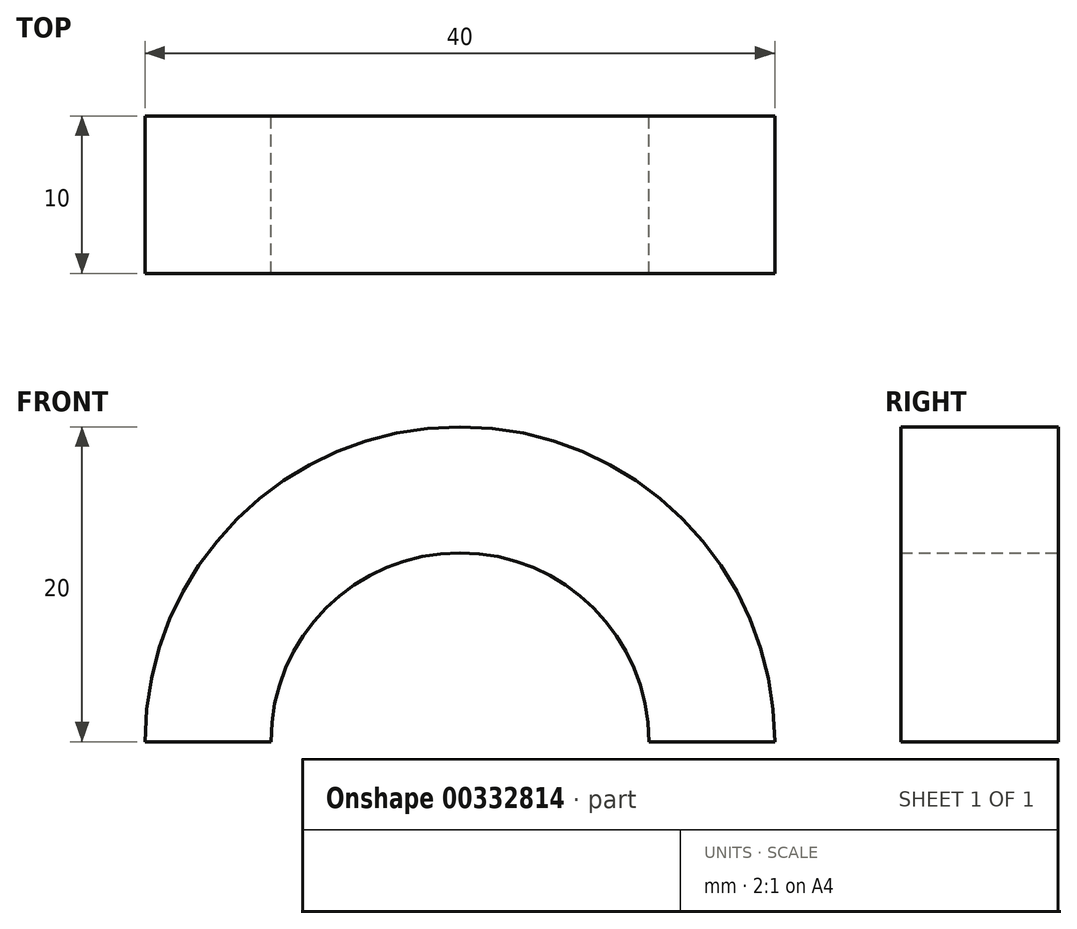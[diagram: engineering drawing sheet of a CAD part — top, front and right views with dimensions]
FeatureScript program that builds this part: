
annotation { "Feature Type Name" : "Feature", "Feature Type Description" : "" }
export const myFeature = defineFeature(function(context is Context, id is Id, definition is map)
    precondition{}
    {
        {
            var Q0;
            Q0=qCreatedBy(makeId("Front.planeOp"),FACE);
            var sketch = newSketch(context, id + "F0", { "sketchPlane" : qUnion([Q0])});
            skCircle(sketch, "E0", {"center": v(0, 0) * mm, "radius": 20 * mm});
            skCircle(sketch, "E1", {"center": v(0, 0) * mm, "radius": 12 * mm});
            skSolve(sketch);
        }
        {
            var Q0;
            Q0 = qSketchRegion(id + "F0", true);
            extrude(context, id + "F1", {"entities" : qUnion([Q0]), "depth" : 10 * mm});
        }
        {
            var Q0;
            Q0=makeQuery(id+"F1.opExtrude","CAP_FACE",FACE,{"disambiguationData":[OSD([sQuery(id+"F0.wireOp",EDGE,"E0"),sQuery(id+"F0.wireOp",EDGE,"E1")])],"isStart":false});
            var sketch = newSketch(context, id + "F2", { "sketchPlane" : qUnion([Q0])});
            skLineSegment(sketch, "E2.bottom", {"start": v(0, 0) * mm, "end": v(-31.6, 0) * mm});
            skLineSegment(sketch, "E2.top", {"start": v(0, -31.13) * mm, "end": v(-31.6, -31.13) * mm});
            skLineSegment(sketch, "E2.left", {"start": v(0, 0) * mm, "end": v(0, -31.13) * mm});
            skLineSegment(sketch, "E2.right", {"start": v(-31.6, 0) * mm, "end": v(-31.6, -31.13) * mm});
            skLineSegment(sketch, "E3.bottom", {"start": v(0, 0) * mm, "end": v(32.65, 0) * mm});
            skLineSegment(sketch, "E3.top", {"start": v(0, -31.13) * mm, "end": v(32.65, -31.13) * mm});
            skLineSegment(sketch, "E3.right", {"start": v(32.65, 0) * mm, "end": v(32.65, -31.13) * mm});
            skSolve(sketch);
        }
        {
            var Q0;
            Q0 = qSketchRegion(id + "F2", true);
            extrude(context, id + "F3", {"entities" : qUnion([Q0]), "operationType" : NewBodyOperationType.REMOVE, "oppositeDirection" : true, "depth" : 25 * mm});
        }
    });
